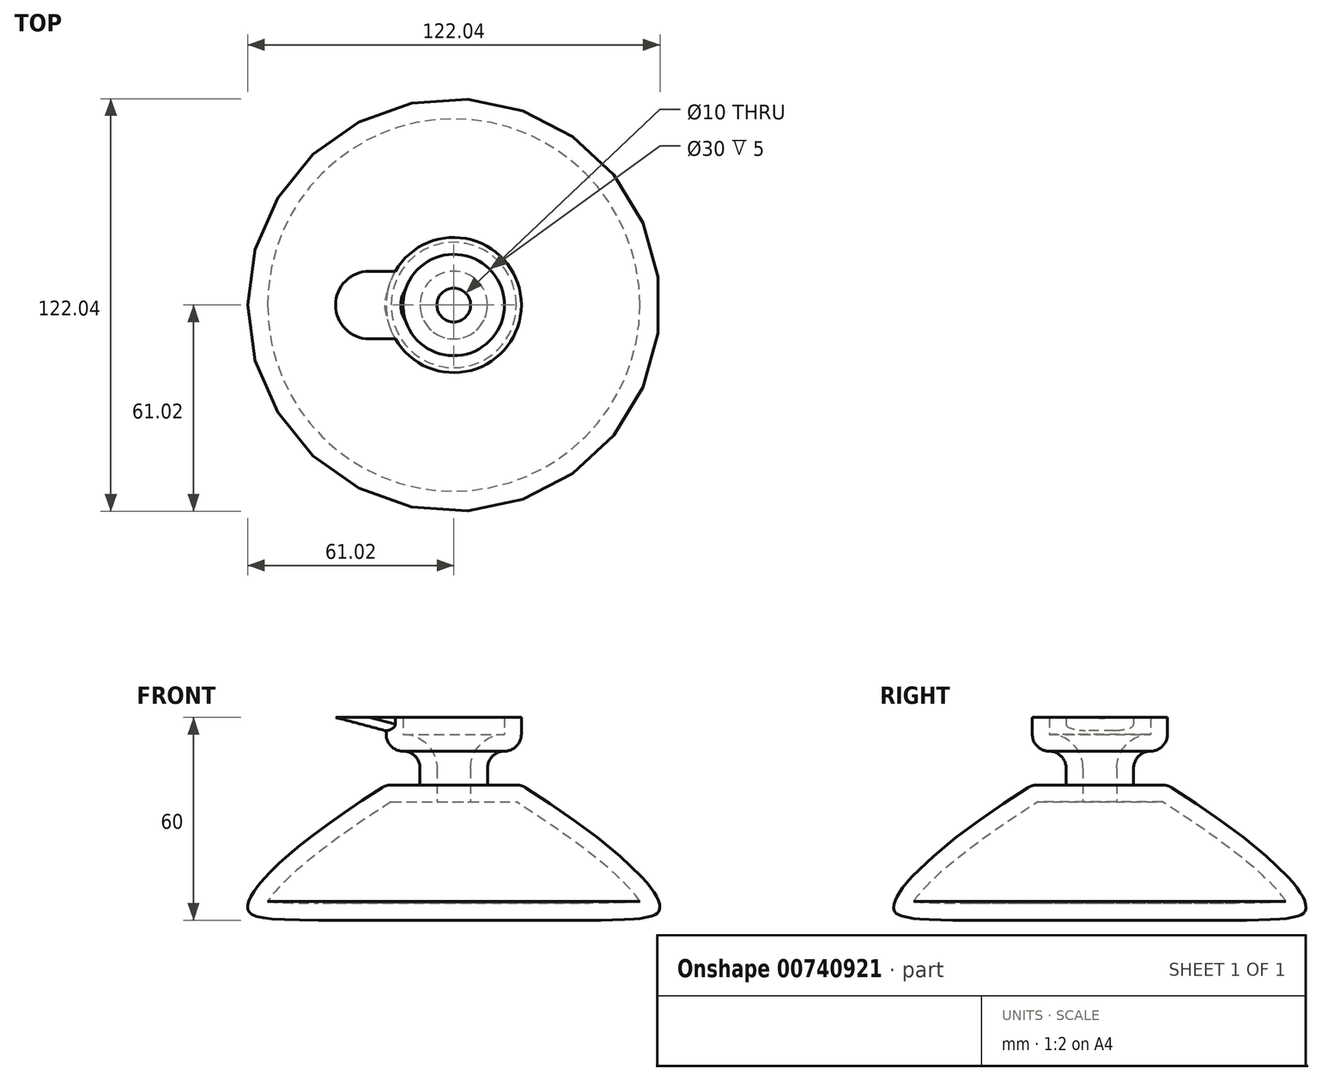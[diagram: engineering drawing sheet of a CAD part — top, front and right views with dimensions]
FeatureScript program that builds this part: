
annotation { "Feature Type Name" : "Feature", "Feature Type Description" : "" }
export const myFeature = defineFeature(function(context is Context, id is Id, definition is map)
    precondition{}
    {
        {
            var Q0;
            Q0=qCreatedBy(makeId("Front.planeOp"),FACE);
            var sketch = newSketch(context, id + "F0", { "sketchPlane" : qUnion([Q0])});
            skLineSegment(sketch, "E0", {"start": v(40, 0) * mm, "end": v(0, 0) * mm});
            skLineSegment(sketch, "E1", {"start": v(0, 0) * mm, "end": v(0, 60) * mm});
            skLineSegment(sketch, "E2", {"start": v(0, 60) * mm, "end": v(20, 60) * mm});
            skLineSegment(sketch, "E3", {"start": v(20, 60) * mm, "end": v(20, 50) * mm});
            skLineSegment(sketch, "E4", {"start": v(20, 50) * mm, "end": v(10, 50) * mm});
            skLineSegment(sketch, "E5", {"start": v(10, 50) * mm, "end": v(10, 40) * mm});
            skLineSegment(sketch, "E6", {"start": v(10, 40) * mm, "end": v(20, 40) * mm});
            skFitSpline(sketch, "E7", {"points": [v(20, 40) * mm, v(60.98, 4.3) * mm, v(40, 0) * mm], "startDerivative": vector(146.66, -93.14) * mm, "endDerivative": vector(-141.62, 0) * mm});
            skSolve(sketch);
        }
        {
            var Q0;
            Q0 = qSketchRegion(id + "F0", true);
            var Q1;
            Q1=sQuery(id+"F0.wireOp",EDGE,"E1");
            revolve(context, id + "F1", {"surfaceOperationType" : NewSurfaceOperationType.NEW, "entities" : qUnion([Q0]), "axis" : qUnion([Q1]), "revolveType" : RevolveType.FULL});
        }
        {
            var Q0;
            Q0=makeQuery(id+"F1.opRevolve","SWEPT_EDGE",EDGE,{"disambiguationData":[OSD([sQuery(id+"F0.wireOp",EDGE,"E6"),sQuery(id+"F0.wireOp",EDGE,"E7")])]});
            var Q1;
            Q1=makeQuery(id+"F1.opRevolve","SWEPT_EDGE",EDGE,{"disambiguationData":[OSD([sQuery(id+"F0.wireOp",EDGE,"E4"),sQuery(id+"F0.wireOp",EDGE,"E5")])]});
            var Q2;
            Q2=makeQuery(id+"F1.opRevolve","SWEPT_EDGE",EDGE,{"disambiguationData":[OSD([sQuery(id+"F0.wireOp",EDGE,"E3"),sQuery(id+"F0.wireOp",EDGE,"E4")])]});
            var Q3;
            Q3=makeQuery(id+"F1.opRevolve","SWEPT_FACE",FACE,{"disambiguationData":[OSD([sQuery(id+"F0.wireOp",EDGE,"E4")])]});
            fillet(context, id + "F2", {"entities" : qUnion([Q0, Q1, Q2, Q3]), "radius" : 5 * mm, "tangentPropagation" : true, "allowEdgeOverflow" : false});
        }
        {
            var Q0;
            Q0=makeQuery(id+"F1.opRevolve","SWEPT_FACE",FACE,{"disambiguationData":[OSD([sQuery(id+"F0.wireOp",EDGE,"E2")])]});
            var sketch = newSketch(context, id + "F3", { "sketchPlane" : qUnion([Q0])});
            skArc(sketch, "E8", {"start": v(-35, 0) * mm, "mid": v(-32.07, -7.07) * mm, "end": v(-25, -10) * mm});
            skLineSegment(sketch, "E9", {"start": v(0, 0) * mm, "end": v(0, -10) * mm});
            skLineSegment(sketch, "E10", {"start": v(0, -10) * mm, "end": v(-25, -10) * mm});
            skArc(sketch, "E11.MirrorCS", {"start": v(-35, 0) * mm, "mid": v(-32.07, 7.07) * mm, "end": v(-25, 10) * mm});
            skLineSegment(sketch, "E12.MirrorCS", {"start": v(0, 10) * mm, "end": v(-25, 10) * mm});
            skLineSegment(sketch, "E13.MirrorCS", {"start": v(0, 0) * mm, "end": v(0, 10) * mm});
            skSolve(sketch);
        }
        {
            var Q0;
            Q0=qCreatedBy(makeId("Front.planeOp"),FACE);
            var sketch = newSketch(context, id + "F4", { "sketchPlane" : qUnion([Q0])});
            skLineSegment(sketch, "E14", {"start": v(0, 60) * mm, "end": v(14.49, 56.12) * mm});
            skSolve(sketch);
        }
        {
            var Q0;
            Q0 = qSketchRegion(id + "F3", true);
            var Q1;
            Q1 = qConstructionFilter(qBodyType(qCreatedBy(id + "F4" ,EDGE), BodyType.WIRE), ConstructionObject.NO);
            sweep(context, id + "F5", {"operationType" : NewBodyOperationType.ADD, "profiles" : qUnion([Q0]), "path" : qUnion([Q1])});
        }
        {
            var Q0;
            Q0=makeQuery(id+"F5.boolean.opBoolean","MERGE",FACE,{"derivedFrom":[makeQuery(id+"F1.opRevolve","SWEPT_FACE",FACE,{"disambiguationData":[OSD([sQuery(id+"F0.wireOp",EDGE,"E2")])]}),makeQuery(id+"F5.opSweep","CAP_FACE",FACE,{"disambiguationData":[OSD([sQuery(id+"F3.wireOp",EDGE,"E8"),sQuery(id+"F3.wireOp",EDGE,"E9"),sQuery(id+"F3.wireOp",EDGE,"E10"),sQuery(id+"F3.wireOp",EDGE,"E11.MirrorCS"),sQuery(id+"F3.wireOp",EDGE,"E12.MirrorCS"),sQuery(id+"F3.wireOp",EDGE,"E13.MirrorCS"),sQuery(id+"F4.wireOp",VERTEX,"E14.start")])],"isStart":true})]});
            shell(context, id + "F6", {"entities" : qUnion([Q0]), "thickness" : 5 * mm});
        }
    });
